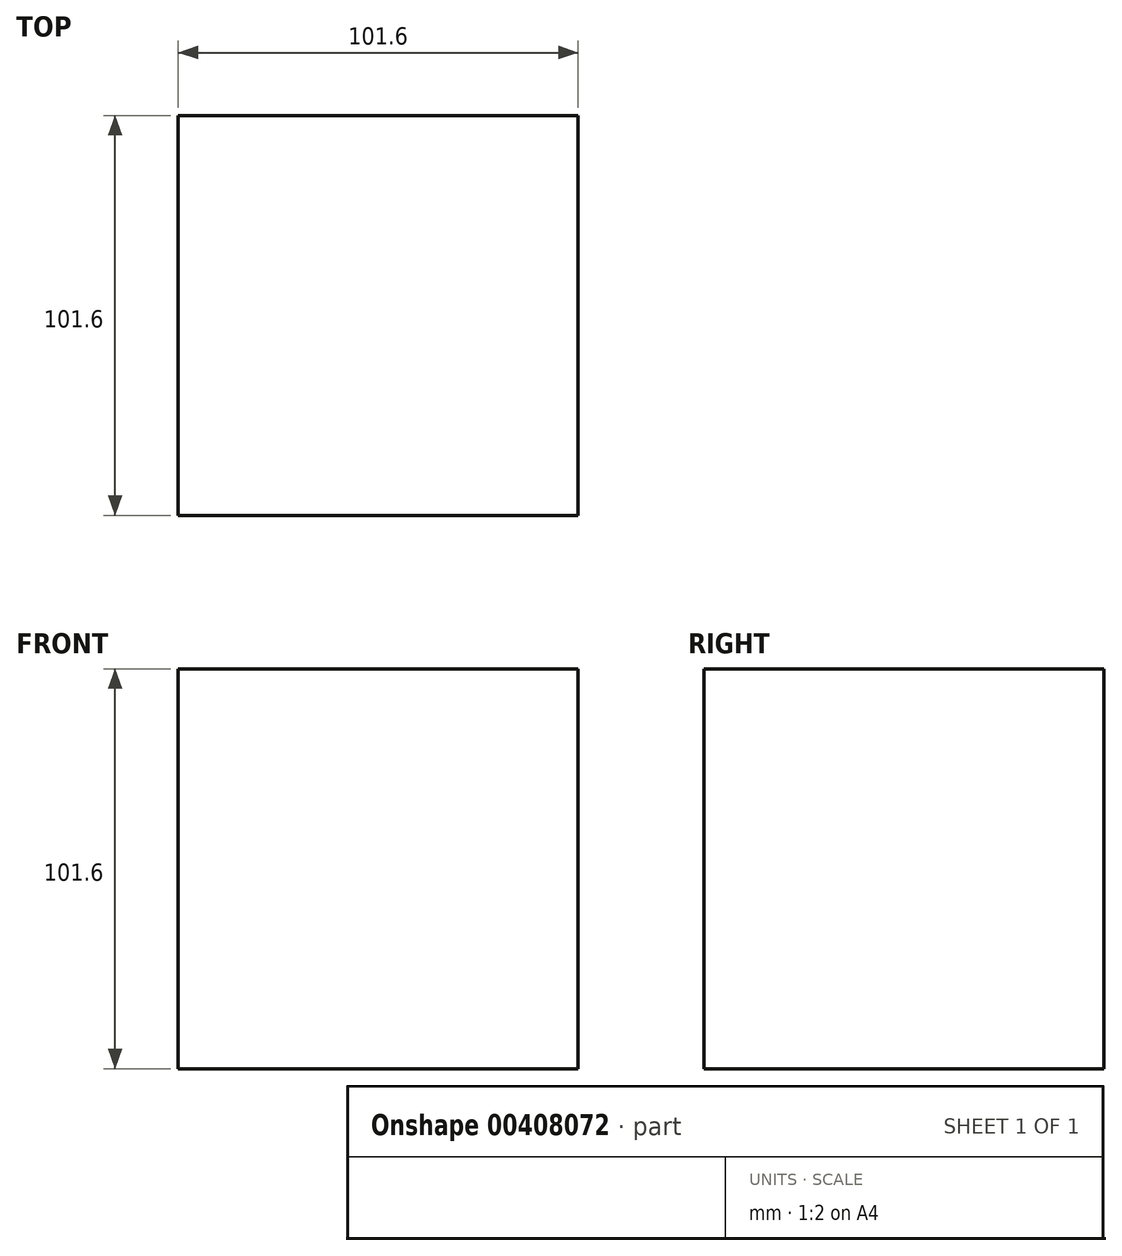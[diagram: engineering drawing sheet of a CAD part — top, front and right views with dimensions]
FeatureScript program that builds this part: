
annotation { "Feature Type Name" : "Feature", "Feature Type Description" : "" }
export const myFeature = defineFeature(function(context is Context, id is Id, definition is map)
    precondition{}
    {
        {
            var Q0;
            Q0=qCreatedBy(makeId("Top.planeOp"),FACE);
            var sketch = newSketch(context, id + "F0", { "sketchPlane" : qUnion([Q0])});
            skLineSegment(sketch, "E0.bottom", {"start": v(-25.4, 25.4) * mm, "end": v(25.4, 25.4) * mm});
            skLineSegment(sketch, "E0.top", {"start": v(-25.4, -25.4) * mm, "end": v(25.4, -25.4) * mm});
            skLineSegment(sketch, "E0.left", {"start": v(-25.4, 25.4) * mm, "end": v(-25.4, -25.4) * mm});
            skLineSegment(sketch, "E0.right", {"start": v(25.4, 25.4) * mm, "end": v(25.4, -25.4) * mm});
            skLineSegment(sketch, "E1", {"start": v(-42.1, 0) * mm, "end": v(-135.68, 0) * mm});
            skSolve(sketch);
        }
        {
            var Q0;
            Q0=makeQuery(id+"F0.imprint","IMPRINT",FACE,{"disambiguationData":[TD([[makeQuery(id+"F0.imprint","IMPRINT",EDGE,{"derivedFrom":sQuery(id+"F0.wireOp",EDGE,"E0.bottom")}),-1.0]])]});
            extrude(context, id + "F1", {"entities" : qUnion([Q0]), "depth" : 50.8 * mm});
        }
        {
            var Q0;
            Q0=makeQuery(id+"F1.opExtrude","SWEPT_BODY",BODY,{"disambiguationData":[OSD([sQuery(id+"F0.wireOp",EDGE,"E0.bottom"),sQuery(id+"F0.wireOp",EDGE,"E0.top"),sQuery(id+"F0.wireOp",EDGE,"E0.left"),sQuery(id+"F0.wireOp",EDGE,"E0.right")])]});
            var Q1;
            Q1=sQuery(id+"F0.wireOp",EDGE,"E1");
            transform(context, id + "F2", {"entities" : qUnion([Q0]), "transformType" : TransformType.TRANSLATION_ENTITY, "oppositeDirectionEntity" : false, "transformLine" : qUnion([Q1]), "makeCopy" : false});
        }
        {
            var Q0;
            Q0=makeQuery(id+"F1.opExtrude","SWEPT_BODY",BODY,{"disambiguationData":[OSD([sQuery(id+"F0.wireOp",EDGE,"E0.bottom"),sQuery(id+"F0.wireOp",EDGE,"E0.top"),sQuery(id+"F0.wireOp",EDGE,"E0.left"),sQuery(id+"F0.wireOp",EDGE,"E0.right")])]});
            var Q1;
            Q1=sQuery(id+"F0.wireOp",EDGE,"E1");
            var Q2;
            Q2=sQuery(id+"F0.wireOp",VERTEX,"E1.start");
            transform(context, id + "F3", {"entities" : qUnion([Q0]), "transformType" : TransformType.SCALE_UNIFORMLY, "scale" : 2, "scalePoint" : qUnion([Q2]), "makeCopy" : false});
        }
    });
